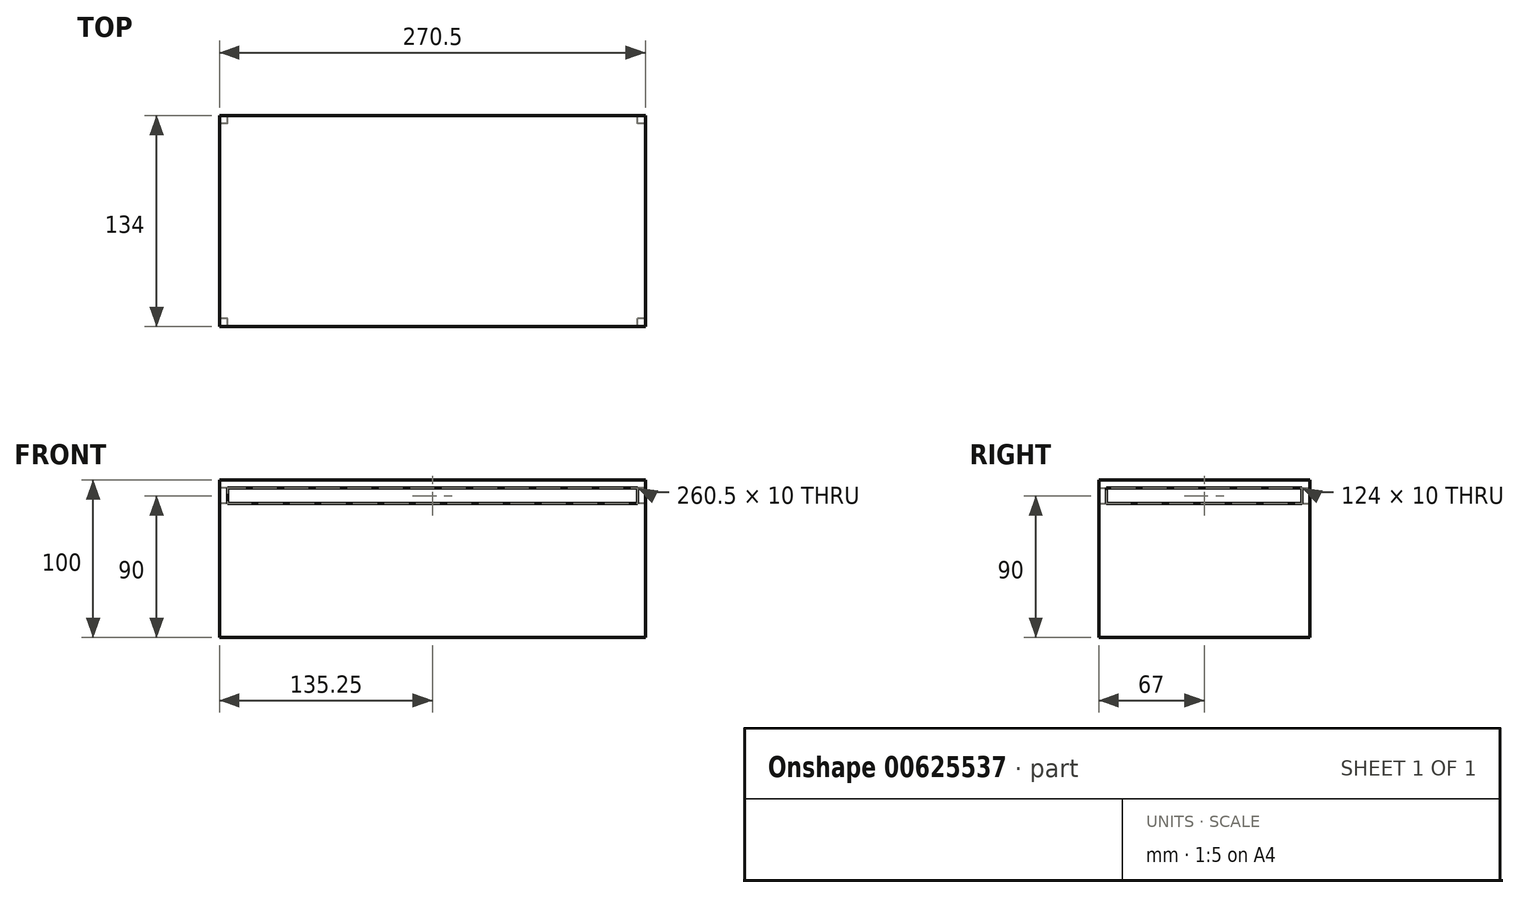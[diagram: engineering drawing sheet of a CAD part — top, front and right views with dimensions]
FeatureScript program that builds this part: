
annotation { "Feature Type Name" : "Feature", "Feature Type Description" : "" }
export const myFeature = defineFeature(function(context is Context, id is Id, definition is map)
    precondition{}
    {
        {
            var Q0;
            Q0=qCreatedBy(makeId("Top.planeOp"),FACE);
            var sketch = newSketch(context, id + "F0", { "sketchPlane" : qUnion([Q0])});
            skLineSegment(sketch, "E0.bottom", {"start": v(-135.25, 67) * mm, "end": v(135.25, 67) * mm});
            skLineSegment(sketch, "E0.top", {"start": v(-135.25, -67) * mm, "end": v(135.25, -67) * mm});
            skLineSegment(sketch, "E0.left", {"start": v(-135.25, 67) * mm, "end": v(-135.25, -67) * mm});
            skLineSegment(sketch, "E0.right", {"start": v(135.25, 67) * mm, "end": v(135.25, -67) * mm});
            skPoint(sketch, "E0.middle", {"position": v(0, 0) * mm});
            skSolve(sketch);
        }
        {
            var Q0;
            Q0=makeQuery(id+"F0.imprint","IMPRINT",FACE,{"disambiguationData":[TD([[makeQuery(id+"F0.imprint","IMPRINT",EDGE,{"derivedFrom":sQuery(id+"F0.wireOp",EDGE,"E0.bottom")}),-1.0]])]});
            extrude(context, id + "F1", {"entities" : qUnion([Q0]), "depth" : 100 * mm, "offsetDistance" : 25 * mm});
        }
        {
            var Q0;
            Q0=makeQuery(id+"F1.opExtrude","SWEPT_FACE",FACE,{"disambiguationData":[OSD([sQuery(id+"F0.wireOp",EDGE,"E0.left")])]});
            var sketch = newSketch(context, id + "F2", { "sketchPlane" : qUnion([Q0])});
            skLineSegment(sketch, "E1.bottom", {"start": v(-62, 95) * mm, "end": v(62, 95) * mm});
            skLineSegment(sketch, "E1.top", {"start": v(-62, 85) * mm, "end": v(62, 85) * mm});
            skLineSegment(sketch, "E1.left", {"start": v(-62, 95) * mm, "end": v(-62, 85) * mm});
            skLineSegment(sketch, "E1.right", {"start": v(62, 95) * mm, "end": v(62, 85) * mm});
            skSolve(sketch);
        }
        {
            var Q0;
            Q0=makeQuery(id+"F2.imprint","IMPRINT",FACE,{"disambiguationData":[TD([[makeQuery(id+"F2.imprint","IMPRINT",EDGE,{"derivedFrom":sQuery(id+"F2.wireOp",EDGE,"E1.bottom")}),-1.0]])]});
            extrude(context, id + "F3", {"entities" : qUnion([Q0]), "operationType" : NewBodyOperationType.REMOVE, "endBound" : BoundingType.THROUGH_ALL, "oppositeDirection" : true, "depth" : 25 * mm, "offsetDistance" : 25 * mm});
        }
        {
            var Q0;
            Q0=makeQuery(id+"F1.opExtrude","SWEPT_FACE",FACE,{"disambiguationData":[OSD([sQuery(id+"F0.wireOp",EDGE,"E0.bottom")])]});
            var sketch = newSketch(context, id + "F4", { "sketchPlane" : qUnion([Q0])});
            skLineSegment(sketch, "E2.bottom", {"start": v(-130.25, 95) * mm, "end": v(130.25, 95) * mm});
            skLineSegment(sketch, "E2.top", {"start": v(-130.25, 85) * mm, "end": v(130.25, 85) * mm});
            skLineSegment(sketch, "E2.left", {"start": v(-130.25, 95) * mm, "end": v(-130.25, 85) * mm});
            skLineSegment(sketch, "E2.right", {"start": v(130.25, 95) * mm, "end": v(130.25, 85) * mm});
            skSolve(sketch);
        }
        {
            var Q0;
            Q0=makeQuery(id+"F4.imprint","IMPRINT",FACE,{"disambiguationData":[TD([[makeQuery(id+"F4.imprint","IMPRINT",EDGE,{"derivedFrom":sQuery(id+"F4.wireOp",EDGE,"E2.bottom")}),-1.0]])]});
            extrude(context, id + "F5", {"entities" : qUnion([Q0]), "operationType" : NewBodyOperationType.REMOVE, "endBound" : BoundingType.THROUGH_ALL, "oppositeDirection" : true, "depth" : 25 * mm, "offsetDistance" : 25 * mm});
        }
    });
